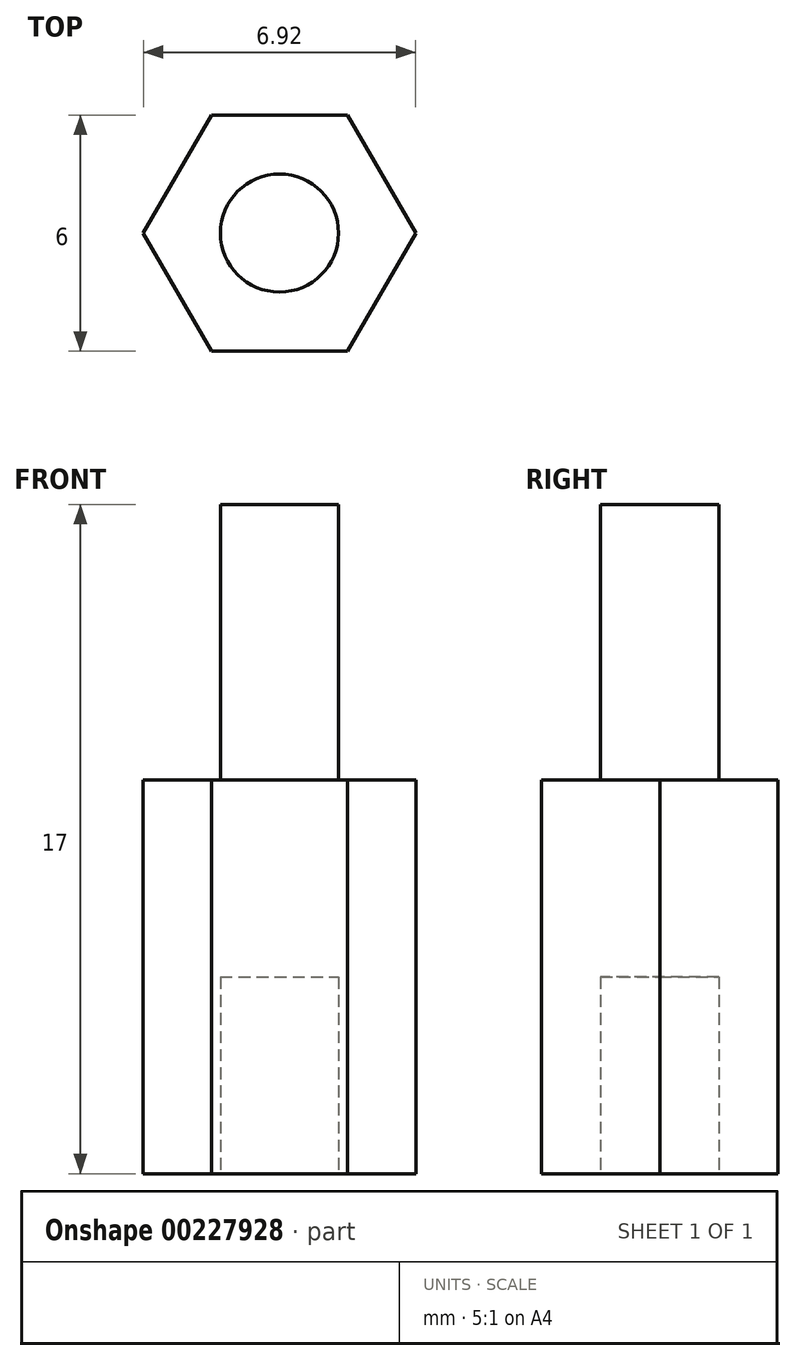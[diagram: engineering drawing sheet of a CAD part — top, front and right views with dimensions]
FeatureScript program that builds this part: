
annotation { "Feature Type Name" : "Feature", "Feature Type Description" : "" }
export const myFeature = defineFeature(function(context is Context, id is Id, definition is map)
    precondition{}
    {
        {
            var Q0;
            Q0=qCreatedBy(makeId("Top.planeOp"),FACE);
            var sketch = newSketch(context, id + "F0", { "sketchPlane" : qUnion([Q0])});
            skCircle(sketch, "E0.cCircle", {"center": v(0, 0) * mm, "radius": 3 * mm, "construction": true});
            skLineSegment(sketch, "E0.0", {"start": v(-1.73, 3) * mm, "end": v(1.73, 3) * mm});
            skLineSegment(sketch, "E0.1", {"start": v(1.73, 3) * mm, "end": v(3.46, 0) * mm});
            skLineSegment(sketch, "E0.2", {"start": v(3.46, 0) * mm, "end": v(1.73, -3) * mm});
            skLineSegment(sketch, "E0.3", {"start": v(1.73, -3) * mm, "end": v(-1.73, -3) * mm});
            skLineSegment(sketch, "E0.4", {"start": v(-1.73, -3) * mm, "end": v(-3.46, 0) * mm});
            skLineSegment(sketch, "E0.5", {"start": v(-3.46, 0) * mm, "end": v(-1.73, 3) * mm});
            skPoint(sketch, "E0.0.midPoint", {"position": v(0, 3) * mm});
            skSolve(sketch);
        }
        {
            var Q0;
            Q0=makeQuery(id+"F0.imprint","IMPRINT",FACE,{"disambiguationData":[TD([[makeQuery(id+"F0.imprint","IMPRINT",EDGE,{"derivedFrom":sQuery(id+"F0.wireOp",EDGE,"E0.0")}),-1.0]])]});
            extrude(context, id + "F1", {"entities" : qUnion([Q0]), "depth" : 10 * mm});
        }
        {
            var Q0;
            Q0=makeQuery(id+"F1.opExtrude","CAP_FACE",FACE,{"disambiguationData":[OSD([sQuery(id+"F0.wireOp",EDGE,"E0.0"),sQuery(id+"F0.wireOp",EDGE,"E0.1"),sQuery(id+"F0.wireOp",EDGE,"E0.2"),sQuery(id+"F0.wireOp",EDGE,"E0.3"),sQuery(id+"F0.wireOp",EDGE,"E0.4"),sQuery(id+"F0.wireOp",EDGE,"E0.5")])],"isStart":false});
            var sketch = newSketch(context, id + "F2", { "sketchPlane" : qUnion([Q0])});
            skLineSegment(sketch, "E1", {"start": v(-1.73, 3) * mm, "end": v(1.73, -3) * mm, "construction": true});
            skCircle(sketch, "E2", {"center": v(0, 0) * mm, "radius": 1.5 * mm});
            skSolve(sketch);
        }
        {
            var Q0;
            Q0=makeQuery(id+"F2.imprint","IMPRINT",FACE,{"disambiguationData":[TD([[makeQuery(id+"F2.imprint","IMPRINT",EDGE,{"derivedFrom":sQuery(id+"F2.wireOp",EDGE,"E2")}),1.0]])]});
            extrude(context, id + "F3", {"entities" : qUnion([Q0]), "operationType" : NewBodyOperationType.ADD, "depth" : 7 * mm});
        }
        {
            var Q0;
            Q0=makeQuery(id+"F1.opExtrude","CAP_FACE",FACE,{"disambiguationData":[OSD([sQuery(id+"F0.wireOp",EDGE,"E0.0"),sQuery(id+"F0.wireOp",EDGE,"E0.1"),sQuery(id+"F0.wireOp",EDGE,"E0.2"),sQuery(id+"F0.wireOp",EDGE,"E0.3"),sQuery(id+"F0.wireOp",EDGE,"E0.4"),sQuery(id+"F0.wireOp",EDGE,"E0.5")])],"isStart":true});
            var sketch = newSketch(context, id + "F4", { "sketchPlane" : qUnion([Q0])});
            skLineSegment(sketch, "E3", {"start": v(1.73, -3) * mm, "end": v(-1.73, 3) * mm, "construction": true});
            skCircle(sketch, "E4", {"center": v(0, 0) * mm, "radius": 1.5 * mm});
            skSolve(sketch);
        }
        {
            var Q0;
            Q0 = qSketchRegion(id + "F4", true);
            extrude(context, id + "F5", {"entities" : qUnion([Q0]), "operationType" : NewBodyOperationType.REMOVE, "oppositeDirection" : true, "depth" : 5 * mm});
        }
    });
